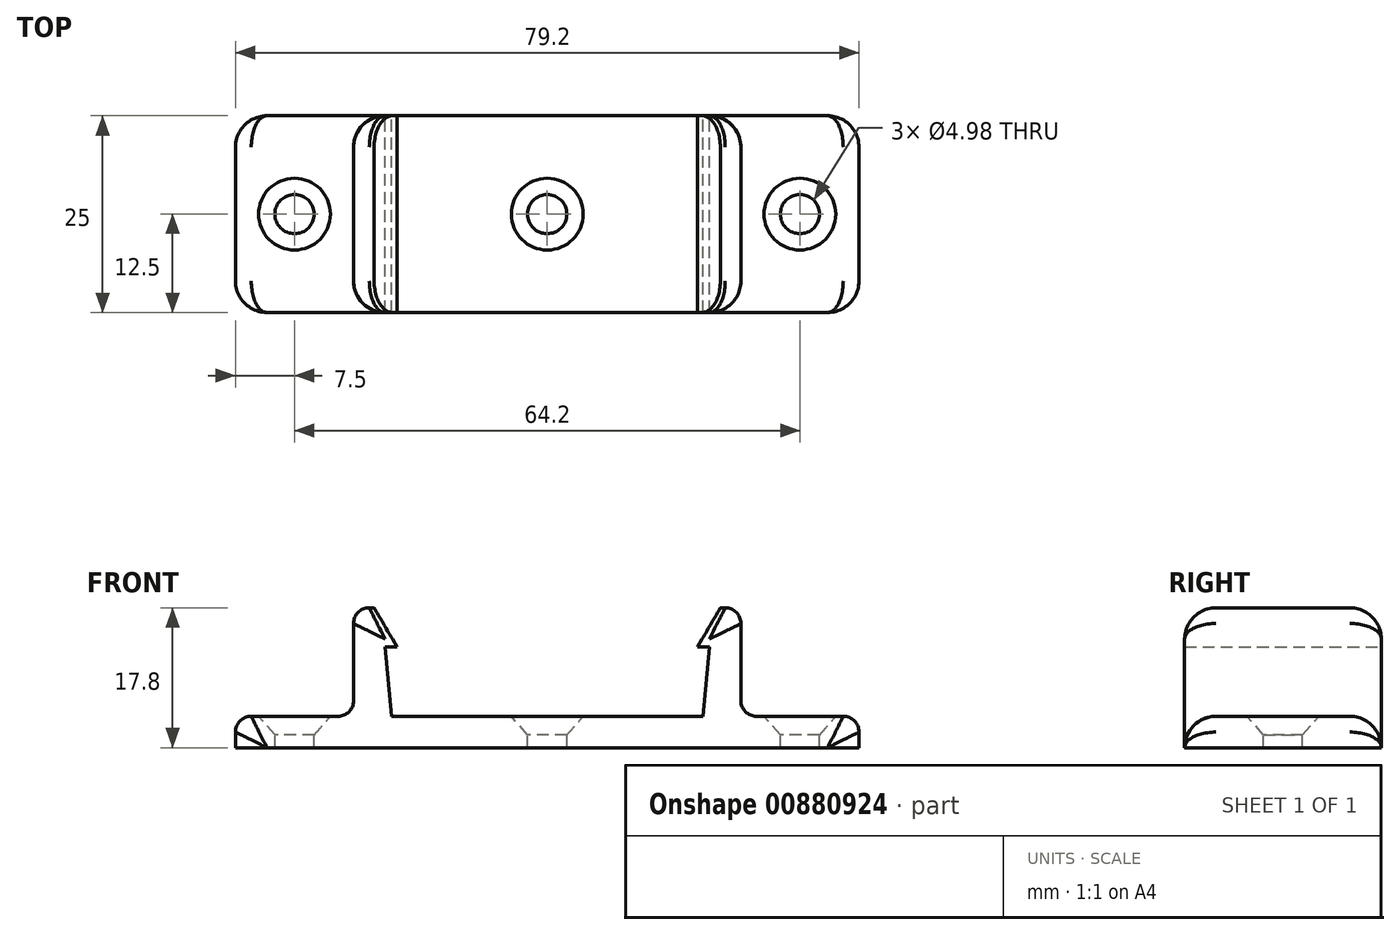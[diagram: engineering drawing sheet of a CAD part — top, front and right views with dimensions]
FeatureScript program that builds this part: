
annotation { "Feature Type Name" : "Feature", "Feature Type Description" : "" }
export const myFeature = defineFeature(function(context is Context, id is Id, definition is map)
    precondition{}
    {
        {
            var Q0;
            Q0=qCreatedBy(makeId("Front.planeOp"),FACE);
            var sketch = newSketch(context, id + "F0", { "sketchPlane" : qUnion([Q0])});
            skLineSegment(sketch, "E0", {"start": v(0, 35.15) * mm, "end": v(0, 0) * mm, "construction": true});
            skLineSegment(sketch, "E1", {"start": v(0, 0) * mm, "end": v(24.6, 0) * mm});
            skLineSegment(sketch, "E2", {"start": v(24.6, 6) * mm, "end": v(24.6, 15.8) * mm});
            skLineSegment(sketch, "E3", {"start": v(22.6, 17.8) * mm, "end": v(21.99, 17.8) * mm});
            skLineSegment(sketch, "E4", {"start": v(21.99, 17.8) * mm, "end": v(19.1, 12.8) * mm});
            skLineSegment(sketch, "E5", {"start": v(19.1, 12.8) * mm, "end": v(20.6, 12.8) * mm});
            skLineSegment(sketch, "E6", {"start": v(20.6, 12.8) * mm, "end": v(19.8, 4) * mm});
            skLineSegment(sketch, "E7", {"start": v(19.8, 4) * mm, "end": v(0, 4) * mm});
            skLineSegment(sketch, "E8.bottom", {"start": v(24.6, 0) * mm, "end": v(39.6, 0) * mm});
            skLineSegment(sketch, "E8.top", {"start": v(26.6, 4) * mm, "end": v(37.6, 4) * mm});
            skLineSegment(sketch, "E8.right", {"start": v(39.6, 0) * mm, "end": v(39.6, 2) * mm});
            skPoint(sketch, "E9.visualSharp", {"position": v(39.6, 4) * mm});
            skArc(sketch, "E9.filletArc", {"start": v(39.6, 2) * mm, "mid": v(39.01, 3.41) * mm, "end": v(37.6, 4) * mm});
            skPoint(sketch, "E10.visualSharp", {"position": v(24.6, 4) * mm});
            skArc(sketch, "E10.filletArc", {"start": v(24.6, 6) * mm, "mid": v(25.19, 4.59) * mm, "end": v(26.6, 4) * mm});
            skPoint(sketch, "E11.visualSharp", {"position": v(24.6, 17.8) * mm});
            skArc(sketch, "E11.filletArc", {"start": v(24.6, 15.8) * mm, "mid": v(24.01, 17.21) * mm, "end": v(22.6, 17.8) * mm});
            skLineSegment(sketch, "E12.MirrorCS", {"start": v(-22.6, 17.8) * mm, "end": v(-21.99, 17.8) * mm});
            skLineSegment(sketch, "E13.MirrorCS", {"start": v(-19.1, 12.8) * mm, "end": v(-20.6, 12.8) * mm});
            skPoint(sketch, "E14.MirrorP", {"position": v(-24.6, 17.8) * mm});
            skLineSegment(sketch, "E15.MirrorCS", {"start": v(-24.6, 6) * mm, "end": v(-24.6, 15.8) * mm});
            skLineSegment(sketch, "E16.MirrorCS", {"start": v(-20.6, 12.8) * mm, "end": v(-19.8, 4) * mm});
            skLineSegment(sketch, "E17.MirrorCS", {"start": v(-39.6, 0) * mm, "end": v(-39.6, 2) * mm});
            skLineSegment(sketch, "E18.MirrorCS", {"start": v(-26.6, 4) * mm, "end": v(-37.6, 4) * mm});
            skLineSegment(sketch, "E19.MirrorCS", {"start": v(0, 0) * mm, "end": v(-24.6, 0) * mm});
            skArc(sketch, "E20.MirrorCS", {"start": v(-39.6, 2) * mm, "mid": v(-39.01, 3.41) * mm, "end": v(-37.6, 4) * mm});
            skArc(sketch, "E21.MirrorCS", {"start": v(-24.6, 6) * mm, "mid": v(-25.19, 4.59) * mm, "end": v(-26.6, 4) * mm});
            skArc(sketch, "E22.MirrorCS", {"start": v(-24.6, 15.8) * mm, "mid": v(-24.01, 17.21) * mm, "end": v(-22.6, 17.8) * mm});
            skPoint(sketch, "E23.MirrorP", {"position": v(-39.6, 4) * mm});
            skPoint(sketch, "E24.MirrorP", {"position": v(-24.6, 4) * mm});
            skLineSegment(sketch, "E25.MirrorCS", {"start": v(-24.6, 0) * mm, "end": v(-39.6, 0) * mm});
            skLineSegment(sketch, "E26.MirrorCS", {"start": v(-19.8, 4) * mm, "end": v(0, 4) * mm});
            skLineSegment(sketch, "E27.MirrorCS", {"start": v(-21.99, 17.8) * mm, "end": v(-19.1, 12.8) * mm});
            skSolve(sketch);
        }
        {
            var Q0;
            Q0 = qSketchRegion(id + "F0", true);
            extrude(context, id + "F1", {"entities" : qUnion([Q0]), "depth" : 25 * mm, "offsetDistance" : 25 * mm});
        }
        {
            var Q0;
            Q0=makeQuery(id+"F1.opExtrude","SWEPT_FACE",FACE,{"disambiguationData":[OSD([sQuery(id+"F0.wireOp",EDGE,"E7"),sQuery(id+"F0.wireOp",EDGE,"E26.MirrorCS")])]});
            var sketch = newSketch(context, id + "F2", { "sketchPlane" : qUnion([Q0])});
            skLineSegment(sketch, "E28", {"start": v(0, -25) * mm, "end": v(0, 0) * mm, "construction": true});
            skPoint(sketch, "E29", {"position": v(0, -12.5) * mm});
            skLineSegment(sketch, "E30.0", {"start": v(-26.6, -25) * mm, "end": v(-26.6, 0) * mm, "construction": true});
            skLineSegment(sketch, "E30.1", {"start": v(-37.6, -25) * mm, "end": v(-37.6, 0) * mm, "construction": true});
            skLineSegment(sketch, "E30.2", {"start": v(26.6, -25) * mm, "end": v(26.6, 0) * mm, "construction": true});
            skLineSegment(sketch, "E30.3", {"start": v(37.6, -25) * mm, "end": v(37.6, 0) * mm, "construction": true});
            skLineSegment(sketch, "E31", {"start": v(-37.6, -12.5) * mm, "end": v(-26.6, -12.5) * mm, "construction": true});
            skLineSegment(sketch, "E32", {"start": v(26.6, -12.5) * mm, "end": v(37.6, -12.5) * mm, "construction": true});
            skPoint(sketch, "E33", {"position": v(-32.1, -12.5) * mm});
            skPoint(sketch, "E34", {"position": v(32.1, -12.5) * mm});
            skSolve(sketch);
        }
        {
            var Q0;
            Q0=sQuery(id+"F2.wireOp",VERTEX,"E33");
            var Q1;
            Q1=sQuery(id+"F2.wireOp",VERTEX,"E29");
            var Q2;
            Q2=sQuery(id+"F2.wireOp",VERTEX,"E34");
            var Q3;
            Q3=makeQuery(id+"F1.opExtrude","SWEPT_BODY",BODY,{"disambiguationData":[OSD([sQuery(id+"F0.wireOp",EDGE,"E1"),sQuery(id+"F0.wireOp",EDGE,"E2"),sQuery(id+"F0.wireOp",EDGE,"E3"),sQuery(id+"F0.wireOp",EDGE,"E4"),sQuery(id+"F0.wireOp",EDGE,"E5"),sQuery(id+"F0.wireOp",EDGE,"E6"),sQuery(id+"F0.wireOp",EDGE,"E7"),sQuery(id+"F0.wireOp",EDGE,"E8.bottom"),sQuery(id+"F0.wireOp",EDGE,"E8.top"),sQuery(id+"F0.wireOp",EDGE,"E8.right"),sQuery(id+"F0.wireOp",EDGE,"E9.filletArc"),sQuery(id+"F0.wireOp",EDGE,"E10.filletArc"),sQuery(id+"F0.wireOp",EDGE,"E11.filletArc"),sQuery(id+"F0.wireOp",EDGE,"E12.MirrorCS"),sQuery(id+"F0.wireOp",EDGE,"E13.MirrorCS"),sQuery(id+"F0.wireOp",EDGE,"E15.MirrorCS"),sQuery(id+"F0.wireOp",EDGE,"E16.MirrorCS"),sQuery(id+"F0.wireOp",EDGE,"E17.MirrorCS"),sQuery(id+"F0.wireOp",EDGE,"E18.MirrorCS"),sQuery(id+"F0.wireOp",EDGE,"E19.MirrorCS"),sQuery(id+"F0.wireOp",EDGE,"E20.MirrorCS"),sQuery(id+"F0.wireOp",EDGE,"E21.MirrorCS"),sQuery(id+"F0.wireOp",EDGE,"E22.MirrorCS"),sQuery(id+"F0.wireOp",EDGE,"E25.MirrorCS"),sQuery(id+"F0.wireOp",EDGE,"E26.MirrorCS"),sQuery(id+"F0.wireOp",EDGE,"E27.MirrorCS")])]});
            hole(context, id + "F3", {"style" : HoleStyle.C_SINK, "endStyle" : HoleEndStyle.THROUGH, "standardTappedOrClearance" : lookupTablePath({ "fit" : "Normal (ASME)", "standard" : "ANSI", "size" : "#8", "type" : "Clearance" }), "standardBlindInLast" : lookupTablePath({ "fit" : "Normal", "standard" : "ANSI", "size" : "#8", "type" : "Clearance" }), "holeDiameter" : 4.98 * mm, "cSinkDiameter" : 9.12 * mm, "cSinkAngle" : 82 * degree, "majorDiameter" : 5 * mm, "isTappedThrough" : true, "tappedDepth" : 12 * mm, "tapClearance" : 3, "locations" : qUnion([Q0, Q1, Q2]), "scope" : qUnion([Q3])});
        }
        {
            var Q0;
            Q0=makeQuery(id+"F1.opExtrude","CAP_EDGE",EDGE,{"disambiguationData":[OSD([sQuery(id+"F0.wireOp",EDGE,"E8.right")])],"isStart":true});
            var Q1;
            Q1=makeQuery(id+"F1.opExtrude","CAP_EDGE",EDGE,{"disambiguationData":[OSD([sQuery(id+"F0.wireOp",EDGE,"E18.MirrorCS")])],"isStart":true});
            var Q2;
            Q2=makeQuery(id+"F1.opExtrude","CAP_EDGE",EDGE,{"disambiguationData":[OSD([sQuery(id+"F0.wireOp",EDGE,"E18.MirrorCS")])],"isStart":false});
            var Q3;
            Q3=makeQuery(id+"F1.opExtrude","CAP_EDGE",EDGE,{"disambiguationData":[OSD([sQuery(id+"F0.wireOp",EDGE,"E8.top")])],"isStart":false});
            fillet(context, id + "F4", {"entities" : qUnion([Q0, Q1, Q2, Q3]), "radius" : 4 * mm, "tangentPropagation" : true, "allowEdgeOverflow" : false});
        }
    });
